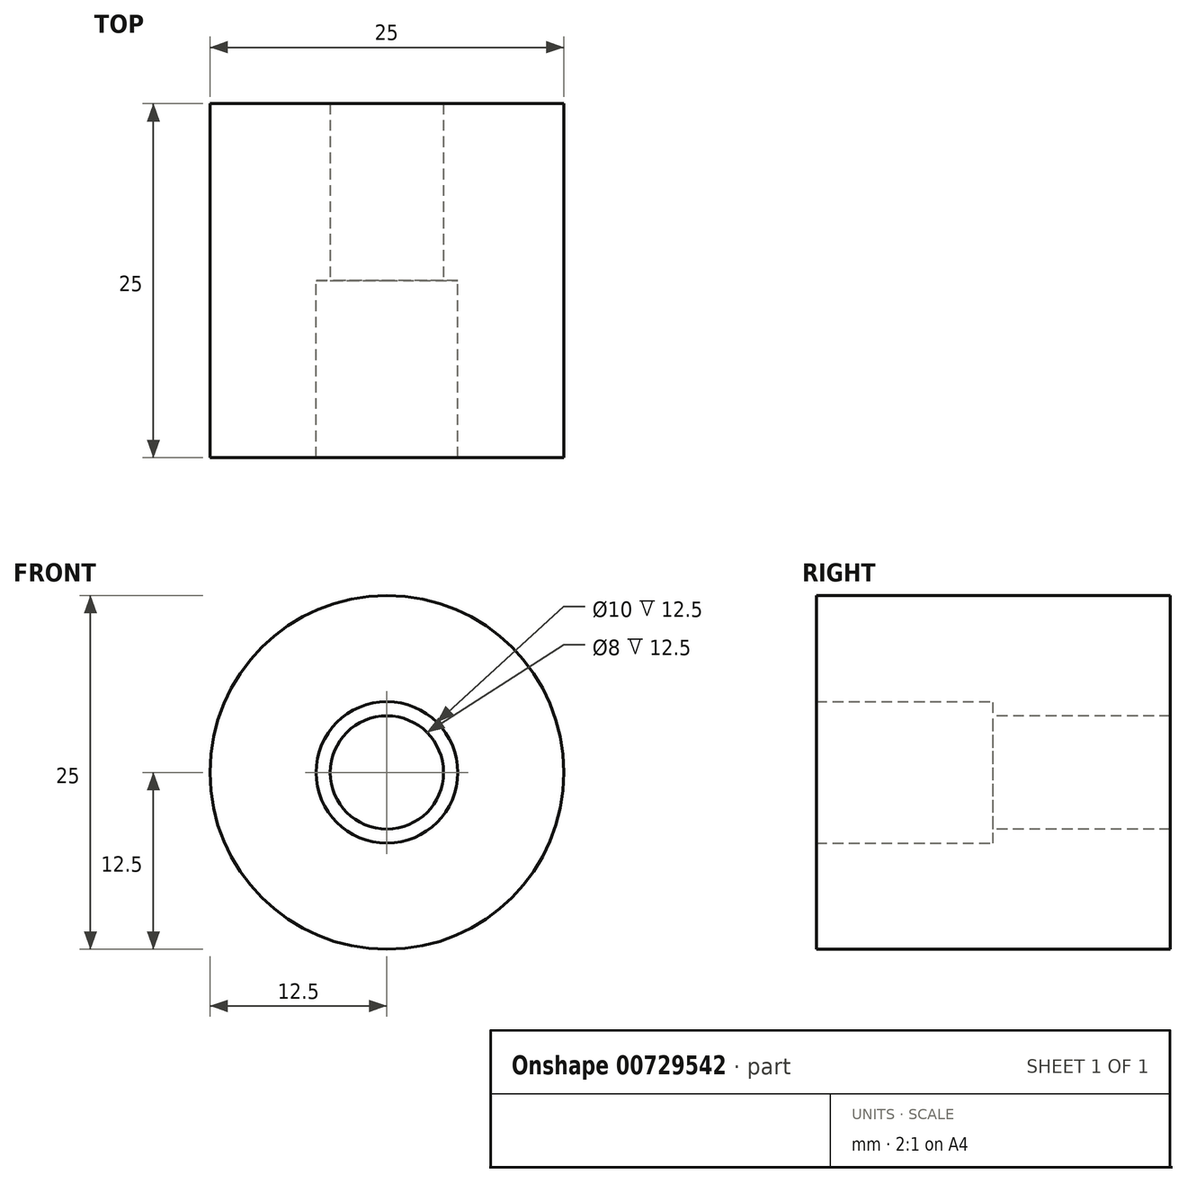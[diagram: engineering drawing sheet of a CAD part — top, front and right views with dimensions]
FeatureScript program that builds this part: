
annotation { "Feature Type Name" : "Feature", "Feature Type Description" : "" }
export const myFeature = defineFeature(function(context is Context, id is Id, definition is map)
    precondition{}
    {
        {
            var Q0;
            Q0=qCreatedBy(makeId("Front.planeOp"),FACE);
            var sketch = newSketch(context, id + "F0", { "sketchPlane" : qUnion([Q0])});
            skCircle(sketch, "E0", {"center": v(0, 0) * mm, "radius": 12.5 * mm});
            skCircle(sketch, "E1", {"center": v(0, 0) * mm, "radius": 5 * mm});
            skCircle(sketch, "E2", {"center": v(0, 0) * mm, "radius": 4 * mm});
            skSolve(sketch);
        }
        {
            var Q0;
            Q0=makeQuery(id+"F0.imprint","IMPRINT",FACE,{"disambiguationData":[TD([[makeQuery(id+"F0.imprint","IMPRINT",EDGE,{"derivedFrom":sQuery(id+"F0.wireOp",EDGE,"E0")}),1.0]])]});
            extrude(context, id + "F1", {"entities" : qUnion([Q0]), "depth" : 12.5 * mm, "offsetDistance" : 25 * mm});
        }
        {
            var Q0;
            Q0=makeQuery(id+"F1.opExtrude","CAP_FACE",FACE,{"disambiguationData":[OSD([sQuery(id+"F0.wireOp",EDGE,"E0"),sQuery(id+"F0.wireOp",EDGE,"E1")])],"isStart":true});
            var Q1;
            Q1=makeQuery(id+"F0.imprint","IMPRINT",FACE,{"disambiguationData":[TD([[makeQuery(id+"F0.imprint","IMPRINT",EDGE,{"derivedFrom":sQuery(id+"F0.wireOp",EDGE,"E1")}),1.0]])]});
            extrude(context, id + "F2", {"entities" : qUnion([Q0, Q1]), "operationType" : NewBodyOperationType.ADD, "depth" : 12.5 * mm, "offsetDistance" : 25 * mm});
        }
    });
